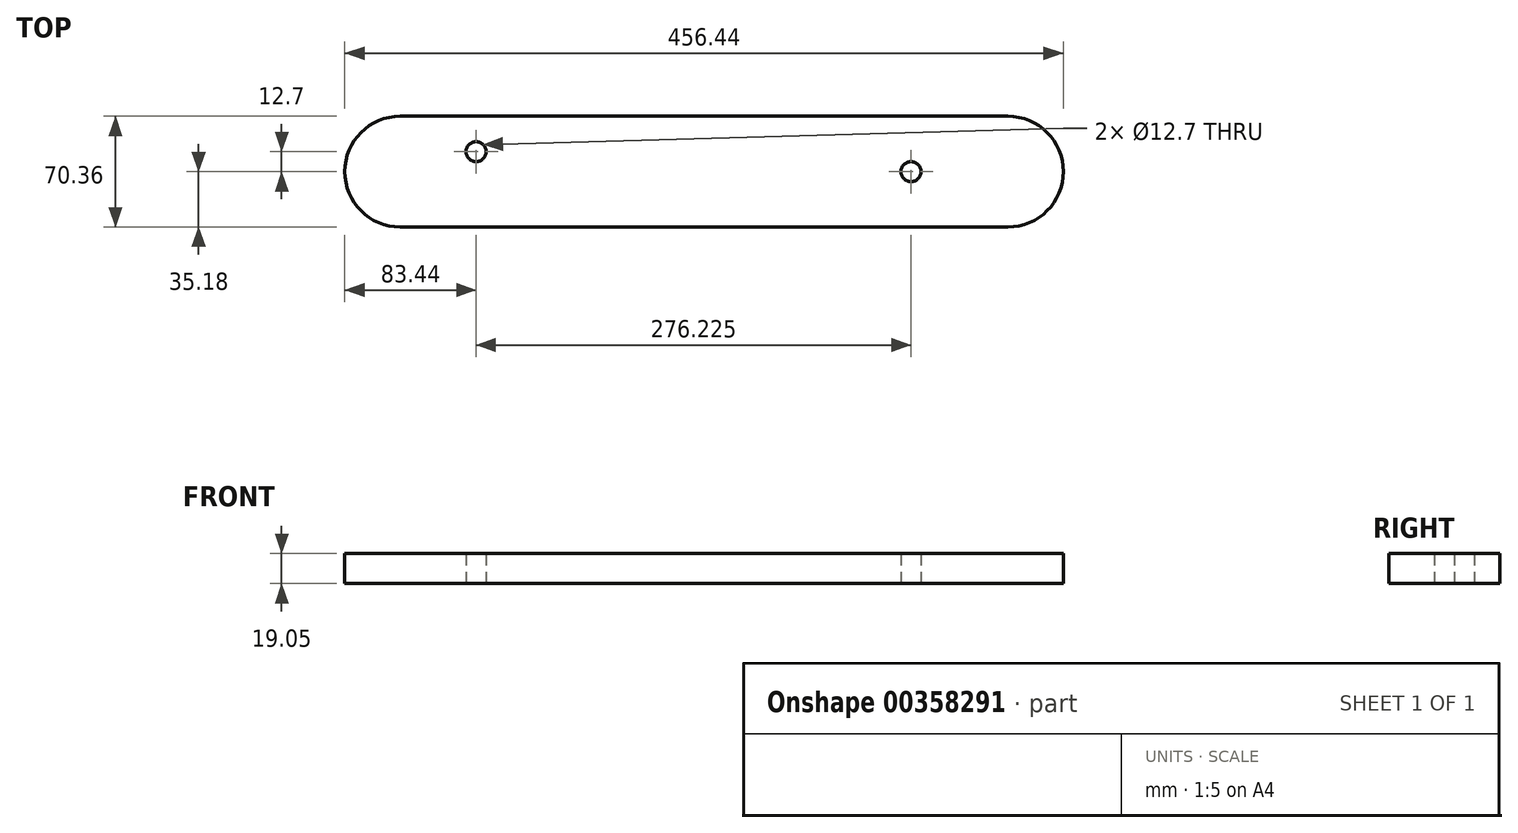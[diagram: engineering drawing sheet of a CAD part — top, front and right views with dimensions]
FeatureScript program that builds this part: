
annotation { "Feature Type Name" : "Feature", "Feature Type Description" : "" }
export const myFeature = defineFeature(function(context is Context, id is Id, definition is map)
    precondition{}
    {
        {
            var Q0;
            Q0=qCreatedBy(makeId("Top.planeOp"),FACE);
            var sketch = newSketch(context, id + "F0", { "sketchPlane" : qUnion([Q0])});
            skCircle(sketch, "E0", {"center": v(0, 0) * mm, "radius": 6.35 * mm});
            skCircle(sketch, "E1", {"center": v(276.23, -12.7) * mm, "radius": 6.35 * mm});
            skArc(sketch, "E2", {"start": v(-48.26, 22.48) * mm, "mid": v(-83.44, -12.7) * mm, "end": v(-48.26, -47.88) * mm});
            skLineSegment(sketch, "E3", {"start": v(373, -47.88) * mm, "end": v(373, 22.48) * mm});
            skLineSegment(sketch, "E4", {"start": v(-48.26, 22.48) * mm, "end": v(373, 22.48) * mm});
            skLineSegment(sketch, "E5", {"start": v(-48.26, -47.88) * mm, "end": v(373, -47.88) * mm});
            skSolve(sketch);
        }
        {
            var Q0;
            Q0 = qSketchRegion(id + "F0", true);
            extrude(context, id + "F1", {"entities" : qUnion([Q0]), "depth" : 19.05 * mm});
        }
        {
            var Q0;
            Q0=makeQuery(id+"F1.opExtrude","SWEPT_EDGE",EDGE,{"disambiguationData":[OSD([sQuery(id+"F0.wireOp",EDGE,"E3"),sQuery(id+"F0.wireOp",EDGE,"E5")])]});
            var Q1;
            Q1=makeQuery(id+"F1.opExtrude","SWEPT_EDGE",EDGE,{"disambiguationData":[OSD([sQuery(id+"F0.wireOp",EDGE,"E3"),sQuery(id+"F0.wireOp",EDGE,"E4")])]});
            fillet(context, id + "F2", {"entities" : qUnion([Q0, Q1]), "radius" : 35.18 * mm, "tangentPropagation" : true, "allowEdgeOverflow" : false});
        }
    });
